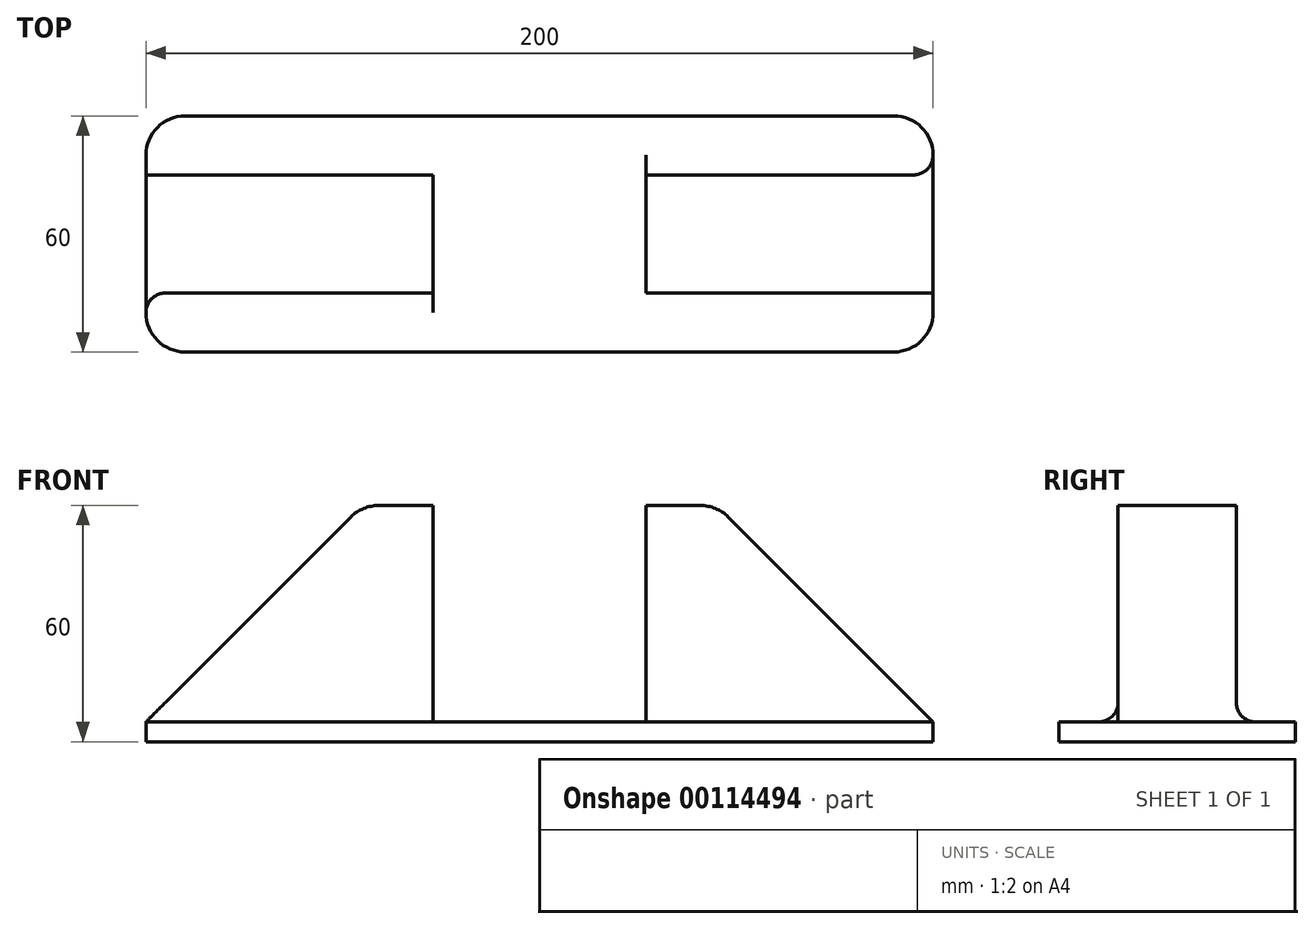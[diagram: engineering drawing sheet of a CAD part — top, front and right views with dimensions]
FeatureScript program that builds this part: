
annotation { "Feature Type Name" : "Feature", "Feature Type Description" : "" }
export const myFeature = defineFeature(function(context is Context, id is Id, definition is map)
    precondition{}
    {
        {
            var Q0;
            Q0=qCreatedBy(makeId("Top.planeOp"),FACE);
            var sketch = newSketch(context, id + "F0", { "sketchPlane" : qUnion([Q0])});
            skLineSegment(sketch, "E0.bottom", {"start": v(-24.93, 22.38) * mm, "end": v(175.07, 22.38) * mm});
            skLineSegment(sketch, "E0.top", {"start": v(-24.93, -7.62) * mm, "end": v(175.07, -7.62) * mm});
            skLineSegment(sketch, "E0.left", {"start": v(-24.93, 22.38) * mm, "end": v(-24.93, -7.62) * mm});
            skLineSegment(sketch, "E0.right", {"start": v(175.07, 22.38) * mm, "end": v(175.07, -7.62) * mm});
            skSolve(sketch);
        }
        {
            var Q0;
            Q0=makeQuery(id+"F0.imprint","IMPRINT",FACE,{"disambiguationData":[TD([[makeQuery(id+"F0.imprint","IMPRINT",EDGE,{"derivedFrom":sQuery(id+"F0.wireOp",EDGE,"E0.bottom")}),-1.0]])]});
            extrude(context, id + "F1", {"entities" : qUnion([Q0]), "depth" : 60 * mm});
        }
        {
            var Q0;
            Q0=makeQuery(id+"F1.opExtrude","CAP_EDGE",EDGE,{"disambiguationData":[OSD([sQuery(id+"F0.wireOp",EDGE,"E0.right")])],"isStart":false});
            chamfer(context, id + "F2", {"entities" : qUnion([Q0]), "width" : 55 * mm, "tangentPropagation" : true});
        }
        {
            var Q0;
            Q0=makeQuery(id+"F1.opExtrude","CAP_EDGE",EDGE,{"disambiguationData":[OSD([sQuery(id+"F0.wireOp",EDGE,"E0.left")])],"isStart":false});
            chamfer(context, id + "F3", {"entities" : qUnion([Q0]), "width" : 55 * mm, "tangentPropagation" : true});
        }
        {
            var Q0;
            Q0=makeQuery(id+"F1.opExtrude","CAP_FACE",FACE,{"disambiguationData":[OSD([sQuery(id+"F0.wireOp",EDGE,"E0.bottom"),sQuery(id+"F0.wireOp",EDGE,"E0.top"),sQuery(id+"F0.wireOp",EDGE,"E0.left"),sQuery(id+"F0.wireOp",EDGE,"E0.right")])],"isStart":false});
            var sketch = newSketch(context, id + "F4", { "sketchPlane" : qUnion([Q0])});
            skLineSegment(sketch, "E1.bottom", {"start": v(48.07, 22.38) * mm, "end": v(102.07, 22.38) * mm});
            skLineSegment(sketch, "E1.top", {"start": v(48.07, -7.62) * mm, "end": v(102.07, -7.62) * mm});
            skLineSegment(sketch, "E1.left", {"start": v(48.07, 22.38) * mm, "end": v(48.07, -7.62) * mm});
            skLineSegment(sketch, "E1.right", {"start": v(102.07, 22.38) * mm, "end": v(102.07, -7.62) * mm});
            skSolve(sketch);
        }
        {
            var Q0;
            Q0=makeQuery(id+"F4.imprint","IMPRINT",FACE,{"disambiguationData":[TD([[makeQuery(id+"F4.imprint","IMPRINT",EDGE,{"derivedFrom":sQuery(id+"F4.wireOp",EDGE,"E1.bottom")}),-1.0]])]});
            extrude(context, id + "F5", {"entities" : qUnion([Q0]), "operationType" : NewBodyOperationType.REMOVE, "oppositeDirection" : true, "depth" : 55 * mm});
        }
        {
            var Q0;
            Q0=makeQuery(id+"F1.opExtrude","SWEPT_FACE",FACE,{"disambiguationData":[OSD([sQuery(id+"F0.wireOp",EDGE,"E0.top")])]});
            var sketch = newSketch(context, id + "F6", { "sketchPlane" : qUnion([Q0])});
            skLineSegment(sketch, "E2.bottom", {"start": v(-24.93, 5) * mm, "end": v(175.07, 5) * mm});
            skLineSegment(sketch, "E2.top", {"start": v(-24.93, 0) * mm, "end": v(175.07, 0) * mm});
            skLineSegment(sketch, "E2.left", {"start": v(-24.93, 5) * mm, "end": v(-24.93, 0) * mm});
            skLineSegment(sketch, "E2.right", {"start": v(175.07, 5) * mm, "end": v(175.07, 0) * mm});
            skSolve(sketch);
        }
        {
            var Q0;
            Q0=makeQuery(id+"F6.imprint","IMPRINT",FACE,{"disambiguationData":[TD([[makeQuery(id+"F6.imprint","IMPRINT",EDGE,{"derivedFrom":sQuery(id+"F6.wireOp",EDGE,"E2.top")}),1.0]])]});
            extrude(context, id + "F7", {"entities" : qUnion([Q0]), "operationType" : NewBodyOperationType.ADD, "depth" : 15 * mm});
        }
        {
            var Q0;
            Q0=makeQuery(id+"F7.opExtrude","CAP_EDGE",EDGE,{"disambiguationData":[OSD([sQuery(id+"F6.wireOp",EDGE,"E2.right")])],"isStart":false});
            var Q1;
            Q1=makeQuery(id+"F7.opExtrude","CAP_EDGE",EDGE,{"disambiguationData":[OSD([sQuery(id+"F6.wireOp",EDGE,"E2.left")])],"isStart":false});
            fillet(context, id + "F8", {"entities" : qUnion([Q0, Q1]), "radius" : 10 * mm, "tangentPropagation" : true, "allowEdgeOverflow" : false});
        }
        {
            var Q0;
            {var subQ1=sQuery(id+"F0.wireOp",EDGE,"E0.right");var subQ2=sQuery(id+"F6.wireOp",EDGE,"E2.bottom");Q0=makeQuery(id+"F7.boolean.opBoolean","SPLIT",EDGE,{"disambiguationData":[TD([makeQuery(id+"F1.opExtrude","SWEPT_FACE",FACE,{"disambiguationData":[OSD([subQ1])]})])],"derivedFrom":makeQuery(id+"F7.opExtrude","CAP_EDGE",EDGE,{"disambiguationData":[OSD([subQ2])],"isStart":true})});}
            var Q1;
            {var subQ1=sQuery(id+"F0.wireOp",EDGE,"E0.left");var subQ2=sQuery(id+"F6.wireOp",EDGE,"E2.bottom");Q1=makeQuery(id+"F7.boolean.opBoolean","SPLIT",EDGE,{"disambiguationData":[TD([makeQuery(id+"F1.opExtrude","SWEPT_FACE",FACE,{"disambiguationData":[OSD([subQ1])]})])],"derivedFrom":makeQuery(id+"F7.opExtrude","CAP_EDGE",EDGE,{"disambiguationData":[OSD([subQ2])],"isStart":true})});}
            fillet(context, id + "F9", {"entities" : qUnion([Q0, Q1]), "radius" : 5 * mm, "tangentPropagation" : true, "allowEdgeOverflow" : false});
        }
        {
            var Q0;
            Q0=makeQuery(id+"F1.opExtrude","SWEPT_FACE",FACE,{"disambiguationData":[OSD([sQuery(id+"F0.wireOp",EDGE,"E0.bottom")])]});
            var sketch = newSketch(context, id + "F10", { "sketchPlane" : qUnion([Q0])});
            skLineSegment(sketch, "E3.bottom", {"start": v(-175.07, 5) * mm, "end": v(24.93, 5) * mm});
            skLineSegment(sketch, "E3.top", {"start": v(-175.07, 0) * mm, "end": v(24.93, 0) * mm});
            skLineSegment(sketch, "E3.left", {"start": v(-175.07, 5) * mm, "end": v(-175.07, 0) * mm});
            skLineSegment(sketch, "E3.right", {"start": v(24.93, 5) * mm, "end": v(24.93, 0) * mm});
            skSolve(sketch);
        }
        {
            var Q0;
            Q0=makeQuery(id+"F10.imprint","IMPRINT",FACE,{"disambiguationData":[TD([[makeQuery(id+"F10.imprint","IMPRINT",EDGE,{"derivedFrom":sQuery(id+"F10.wireOp",EDGE,"E3.top")}),-1.0]])]});
            extrude(context, id + "F11", {"entities" : qUnion([Q0]), "operationType" : NewBodyOperationType.ADD, "depth" : 15 * mm});
        }
        {
            var Q0;
            {var subQ1=sQuery(id+"F0.wireOp",EDGE,"E0.right");var subQ2=sQuery(id+"F10.wireOp",EDGE,"E3.bottom");Q0=makeQuery(id+"F11.boolean.opBoolean","SPLIT",EDGE,{"disambiguationData":[TD([makeQuery(id+"F1.opExtrude","SWEPT_FACE",FACE,{"disambiguationData":[OSD([subQ1])]})])],"derivedFrom":makeQuery(id+"F11.opExtrude","CAP_EDGE",EDGE,{"disambiguationData":[OSD([subQ2])],"isStart":true})});}
            var Q1;
            {var subQ1=sQuery(id+"F0.wireOp",EDGE,"E0.left");var subQ2=sQuery(id+"F10.wireOp",EDGE,"E3.bottom");Q1=makeQuery(id+"F11.boolean.opBoolean","SPLIT",EDGE,{"disambiguationData":[TD([makeQuery(id+"F1.opExtrude","SWEPT_FACE",FACE,{"disambiguationData":[OSD([subQ1])]})])],"derivedFrom":makeQuery(id+"F11.opExtrude","CAP_EDGE",EDGE,{"disambiguationData":[OSD([subQ2])],"isStart":true})});}
            fillet(context, id + "F12", {"entities" : qUnion([Q0, Q1]), "radius" : 5 * mm, "tangentPropagation" : true, "allowEdgeOverflow" : false});
        }
        {
            var Q0;
            Q0=makeQuery(id+"F11.opExtrude","CAP_EDGE",EDGE,{"disambiguationData":[OSD([sQuery(id+"F10.wireOp",EDGE,"E3.left")])],"isStart":false});
            var Q1;
            Q1=makeQuery(id+"F11.opExtrude","CAP_EDGE",EDGE,{"disambiguationData":[OSD([sQuery(id+"F10.wireOp",EDGE,"E3.right")])],"isStart":false});
            var Q2;
            {var subQ0=sQuery(id+"F0.wireOp",EDGE,"E0.right");Q2=makeQuery(id+"F2.opChamfer","BLEND_EDGE",EDGE,{"blendedFrom":[makeQuery(id+"F1.opExtrude","CAP_EDGE",EDGE,{"disambiguationData":[OSD([subQ0])],"isStart":false}),makeQuery(id+"F1.opExtrude","CAP_FACE",FACE,{"disambiguationData":[OSD([sQuery(id+"F0.wireOp",EDGE,"E0.bottom"),sQuery(id+"F0.wireOp",EDGE,"E0.top"),sQuery(id+"F0.wireOp",EDGE,"E0.left"),subQ0])],"isStart":false})],"blendedInto":[makeQuery(id+"F1.opExtrude","CAP_FACE",FACE,{"disambiguationData":[OSD([sQuery(id+"F0.wireOp",EDGE,"E0.bottom"),sQuery(id+"F0.wireOp",EDGE,"E0.top"),sQuery(id+"F0.wireOp",EDGE,"E0.left"),subQ0])],"isStart":false})]});}
            var Q3;
            {var subQ0=sQuery(id+"F0.wireOp",EDGE,"E0.left");Q3=makeQuery(id+"F3.opChamfer","BLEND_EDGE",EDGE,{"blendedFrom":[makeQuery(id+"F1.opExtrude","CAP_EDGE",EDGE,{"disambiguationData":[OSD([subQ0])],"isStart":false}),makeQuery(id+"F1.opExtrude","CAP_FACE",FACE,{"disambiguationData":[OSD([sQuery(id+"F0.wireOp",EDGE,"E0.bottom"),sQuery(id+"F0.wireOp",EDGE,"E0.top"),subQ0,sQuery(id+"F0.wireOp",EDGE,"E0.right")])],"isStart":false})],"blendedInto":[makeQuery(id+"F1.opExtrude","CAP_FACE",FACE,{"disambiguationData":[OSD([sQuery(id+"F0.wireOp",EDGE,"E0.bottom"),sQuery(id+"F0.wireOp",EDGE,"E0.top"),subQ0,sQuery(id+"F0.wireOp",EDGE,"E0.right")])],"isStart":false})]});}
            fillet(context, id + "F13", {"entities" : qUnion([Q0, Q1, Q2, Q3]), "radius" : 10 * mm, "tangentPropagation" : true, "allowEdgeOverflow" : false});
        }
    });
